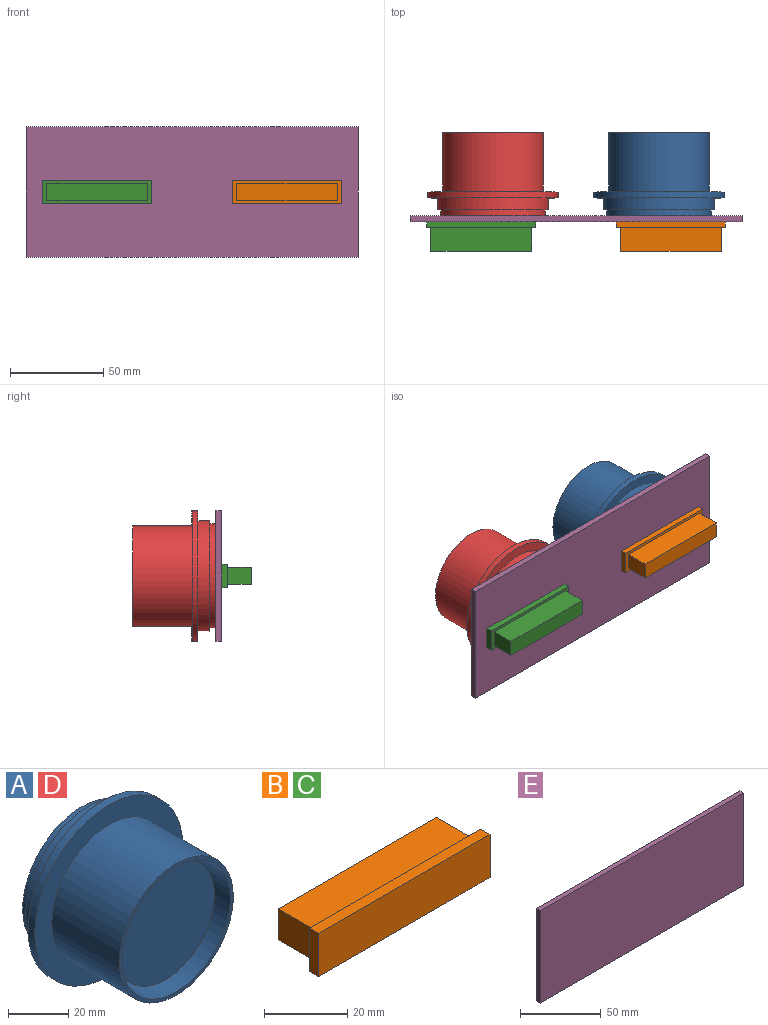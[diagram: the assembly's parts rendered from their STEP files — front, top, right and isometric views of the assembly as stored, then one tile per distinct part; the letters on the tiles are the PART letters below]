
ASSEMBLY  parts=5 mates=4
PART A: 13 faces, bbox 69.9x44.5x69.9 mm
  f0: cylinder r=34.92mm len=69.85mm, axis (0,1,0), area 696.7mm2, adj f1,f2
  f1: plane 69.85x69.85mm, normal (0,-1,0), area 1563.4mm2, adj f0,f3
  f2: plane 69.85x69.85mm, normal (0,1,0), area 1061.7mm2, adj f0,f5
  f3: cylinder r=26.87mm len=53.74mm, axis (0,1,0), area 5360.8mm2, adj f1,f4
  f4: plane 53.74x53.74mm, normal (0,-1,0), area 228.1mm2, adj f3,f9
  f5: cylinder r=29.7mm len=59.39mm, axis (0,-1,0), area 1184.8mm2, adj f2,f6
  f6: plane 59.39x59.39mm, normal (0,1,0), area 324.8mm2, adj f5,f7
  f7: cylinder r=27.9mm len=55.8mm, axis (0,-1,0), area 556.6mm2, adj f6,f8
  f8: plane 55.8x55.8mm, normal (0,1,0), area 2445.5mm2, adj f7
  f9: cylinder r=25.49mm len=50.97mm, axis (0,-1,0), area 4067.3mm2, adj f4,f10
  f10: plane 50.97x50.97mm, normal (0,-1,0), area 365.5mm2, adj f9,f11
  f11: cylinder r=23.09mm len=46.18mm, axis (0,1,0), area 2948.1mm2, adj f10,f12
  f12: plane 46.18x46.18mm, normal (0,-1,0), area 1675mm2, adj f11
PART B: 11 faces, bbox 58.4x15.9x12.7 mm
  f0: plane 58.42x3.18mm, normal (0,0,1), area 185.5mm2, adj f1,f3,f4,f5
  f1: plane 12.7x3.18mm, normal (-1,0,0), area 40.3mm2, adj f0,f2,f4,f5
  f2: plane 58.42x3.18mm, normal (0,0,-1), area 185.5mm2, adj f1,f3,f4,f5
  f3: plane 12.7x3.18mm, normal (1,0,0), area 40.3mm2, adj f0,f2,f4,f5
  f4: plane 58.42x12.7mm, normal (0,1,0), area 249.8mm2, adj f0,f1,f2,f3,f6,f7,f8,f9
  f5: plane 58.42x12.7mm, normal (0,-1,0), area 741.9mm2, adj f0,f1,f2,f3
  f6: plane 54.01x12.7mm, normal (0,0,1), area 685.9mm2, adj f4,f7,f9,f10
  f7: plane 12.7x9.11mm, normal (1,0,0), area 115.7mm2, adj f4,f6,f8,f10
  f8: plane 54.01x12.7mm, normal (0,0,-1), area 685.9mm2, adj f4,f7,f9,f10
  f9: plane 12.7x9.11mm, normal (-1,0,0), area 115.7mm2, adj f4,f6,f8,f10
  f10: plane 54.01x9.11mm, normal (0,1,0), area 492.1mm2, adj f6,f7,f8,f9
PART C: same geometry as B
PART D: same geometry as A
PART E: 6 faces, bbox 177.8x3.2x69.9 mm
  f0: plane 177.8x3.18mm, normal (0,0,1), area 564.5mm2, adj f1,f3,f4,f5
  f1: plane 69.85x3.18mm, normal (-1,0,0), area 221.8mm2, adj f0,f2,f4,f5
  f2: plane 177.8x3.18mm, normal (0,0,-1), area 564.5mm2, adj f1,f3,f4,f5
  f3: plane 69.85x3.18mm, normal (1,0,0), area 221.8mm2, adj f0,f2,f4,f5
  f4: plane 177.8x69.85mm, normal (0,1,0), area 12419.3mm2, adj f0,f1,f2,f3
  f5: plane 177.8x69.85mm, normal (0,-1,0), area 12419.3mm2, adj f0,f1,f2,f3
PLACE A rot(axis=(0,0,-1),180deg) t=(-851,-248.27,158.47)mm
PLACE B rot(axis=(0,0,-1),180deg) t=(-638.17,-260.97,61.42)mm
PLACE C rot(axis=(0,0,-1),180deg) t=(-739.77,-260.97,61.42)mm
PLACE D rot(axis=(0,0,-1),180deg) t=(-939.9,-248.27,158.47)mm
PLACE E rot(axis=(0,0,-1),180deg) t=(-625.35,-257.8,158.47)mm
MATE fastened B.f5 <-> E.f4  axis (0,1,0) through (-120.45,-260.97,-15.59)mm
MATE fastened D.f0 <-> E.f5  axis (0,-1,0) through (-215.7,-257.8,-15.59)mm
MATE fastened A.f0 <-> E.f5  axis (0,-1,0) through (-126.8,-257.8,-15.59)mm
MATE fastened C.f5 <-> E.f4  axis (0,1,0) through (-222.05,-260.97,-15.59)mm
